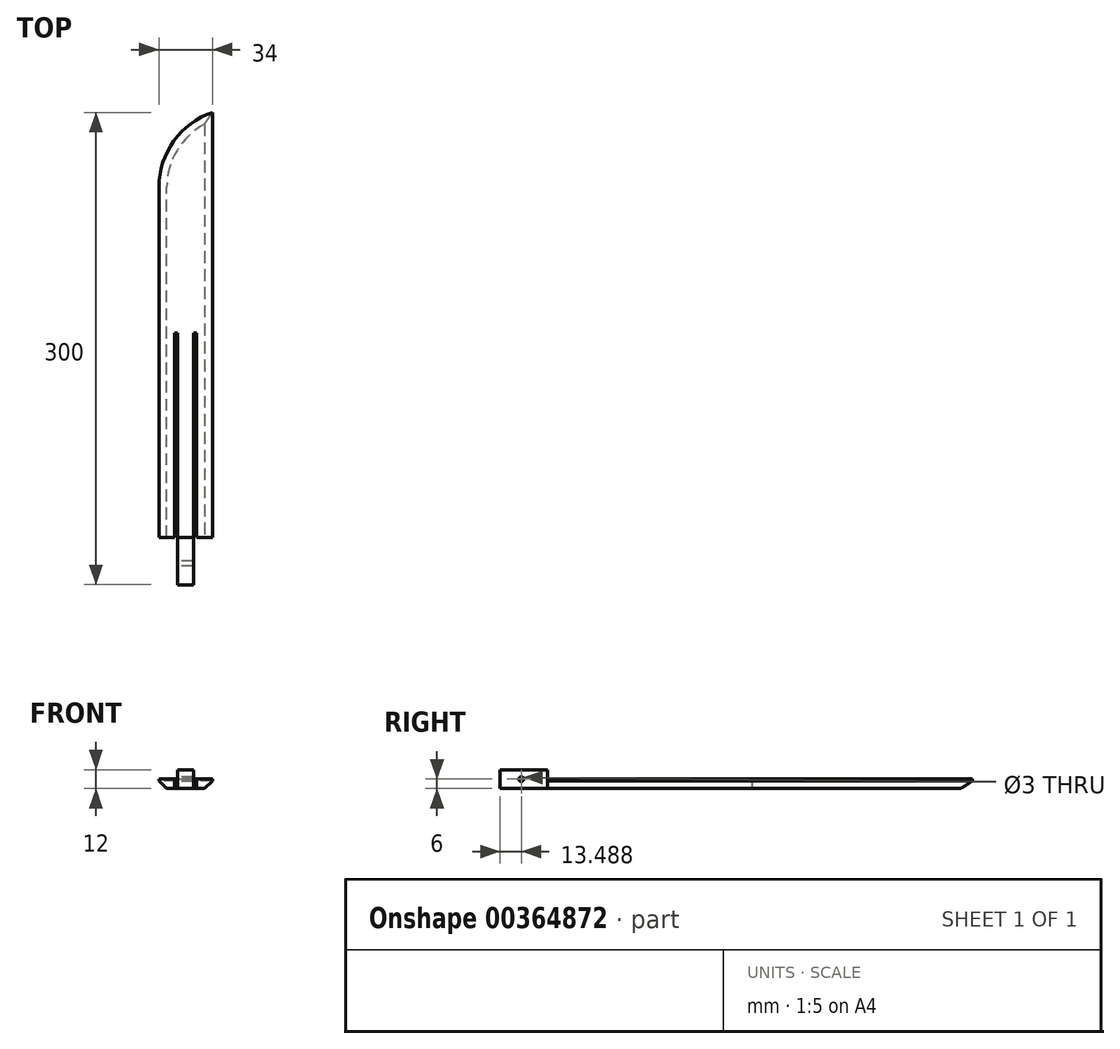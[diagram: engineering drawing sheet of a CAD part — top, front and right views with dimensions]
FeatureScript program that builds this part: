
annotation { "Feature Type Name" : "Feature", "Feature Type Description" : "" }
export const myFeature = defineFeature(function(context is Context, id is Id, definition is map)
    precondition{}
    {
        {
            var Q0;
            Q0=qCreatedBy(makeId("Top.planeOp"),FACE);
            var sketch = newSketch(context, id + "F0", { "sketchPlane" : qUnion([Q0])});
            skLineSegment(sketch, "E0.bottom", {"start": v(-19.09, 227.5) * mm, "end": v(14.91, 227.5) * mm});
            skLineSegment(sketch, "E0.left", {"start": v(-19.09, 227.5) * mm, "end": v(-19.09, -42.5) * mm});
            skLineSegment(sketch, "E0.right", {"start": v(14.91, 227.5) * mm, "end": v(14.91, -42.5) * mm});
            skLineSegment(sketch, "E1.top", {"start": v(-9.09, 87.5) * mm, "end": v(-7.09, 87.5) * mm});
            skLineSegment(sketch, "E1.left", {"start": v(-9.09, -42.5) * mm, "end": v(-9.09, 87.5) * mm});
            skLineSegment(sketch, "E1.right", {"start": v(-7.09, -72.5) * mm, "end": v(-7.09, 87.5) * mm});
            skLineSegment(sketch, "E2.top", {"start": v(2.91, 87.5) * mm, "end": v(4.91, 87.5) * mm});
            skLineSegment(sketch, "E2.left", {"start": v(2.91, -72.5) * mm, "end": v(2.91, 87.5) * mm});
            skLineSegment(sketch, "E2.right", {"start": v(4.91, -42.5) * mm, "end": v(4.91, 87.5) * mm});
            skLineSegment(sketch, "E3.trimOffspring", {"start": v(-7.09, -72.5) * mm, "end": v(2.91, -72.5) * mm});
            skLineSegment(sketch, "E4.top", {"start": v(-19.09, -42.5) * mm, "end": v(-9.09, -42.5) * mm});
            skLineSegment(sketch, "E5.top", {"start": v(4.91, -42.5) * mm, "end": v(14.91, -42.5) * mm});
            skSolve(sketch);
        }
        {
            var Q0;
            Q0=makeQuery(id+"F0.imprint","IMPRINT",FACE,{"disambiguationData":[TD([[makeQuery(id+"F0.imprint","IMPRINT",EDGE,{"derivedFrom":sQuery(id+"F0.wireOp",EDGE,"E0.bottom")}),-1.0]])]});
            extrude(context, id + "F1", {"entities" : qUnion([Q0]), "depth" : 6 * mm});
        }
        {
            var Q0;
            Q0=makeQuery(id+"F1.opExtrude","SWEPT_EDGE",EDGE,{"disambiguationData":[OSD([sQuery(id+"F0.wireOp",EDGE,"E0.bottom"),sQuery(id+"F0.wireOp",EDGE,"E0.left")])]});
            fillet(context, id + "F2", {"entities" : qUnion([Q0]), "radius" : 50 * mm, "tangentPropagation" : true, "allowEdgeOverflow" : false});
        }
        {
            var Q0;
            Q0=makeQuery(id+"F1.opExtrude","CAP_FACE",FACE,{"disambiguationData":[OSD([sQuery(id+"F0.wireOp",EDGE,"E0.bottom"),sQuery(id+"F0.wireOp",EDGE,"E0.left"),sQuery(id+"F0.wireOp",EDGE,"E0.right"),sQuery(id+"F0.wireOp",EDGE,"E1.top"),sQuery(id+"F0.wireOp",EDGE,"E1.left"),sQuery(id+"F0.wireOp",EDGE,"E1.right"),sQuery(id+"F0.wireOp",EDGE,"E2.top"),sQuery(id+"F0.wireOp",EDGE,"E2.left"),sQuery(id+"F0.wireOp",EDGE,"E2.right"),sQuery(id+"F0.wireOp",EDGE,"E3.trimOffspring"),sQuery(id+"F0.wireOp",EDGE,"E4.top"),sQuery(id+"F0.wireOp",EDGE,"E5.top")])],"isStart":false});
            var sketch = newSketch(context, id + "F3", { "sketchPlane" : qUnion([Q0])});
            skLineSegment(sketch, "E6.bottom", {"start": v(-7.09, -42.5) * mm, "end": v(2.91, -42.5) * mm});
            skLineSegment(sketch, "E6.top", {"start": v(-7.09, -72.5) * mm, "end": v(2.91, -72.5) * mm});
            skLineSegment(sketch, "E6.left", {"start": v(-7.09, -42.5) * mm, "end": v(-7.09, -72.5) * mm});
            skLineSegment(sketch, "E6.right", {"start": v(2.91, -42.5) * mm, "end": v(2.91, -72.5) * mm});
            skSolve(sketch);
        }
        {
            var Q0;
            Q0 = qSketchRegion(id + "F3", true);
            extrude(context, id + "F4", {"entities" : qUnion([Q0]), "operationType" : NewBodyOperationType.ADD, "depth" : 6 * mm});
        }
        {
            var Q0;
            Q0=makeQuery(id+"F4.boolean.opBoolean","MERGE",FACE,{"derivedFrom":[makeQuery(id+"F1.opExtrude","SWEPT_FACE",FACE,{"disambiguationData":[OSD([sQuery(id+"F0.wireOp",EDGE,"E1.right")])]}),makeQuery(id+"F4.opExtrude","SWEPT_FACE",FACE,{"disambiguationData":[OSD([sQuery(id+"F3.wireOp",EDGE,"E6.left")])]})]});
            var sketch = newSketch(context, id + "F5", { "sketchPlane" : qUnion([Q0])});
            skCircle(sketch, "E7", {"center": v(59, 6) * mm, "radius": 1.5 * mm});
            skPoint(sketch, "E7.centerSnap0", {"position": v(72.5, 6) * mm});
            skSolve(sketch);
        }
        {
            var Q0;
            Q0=makeQuery(id+"F5.imprint","IMPRINT",FACE,{"disambiguationData":[TD([[makeQuery(id+"F5.imprint","IMPRINT",EDGE,{"derivedFrom":sQuery(id+"F5.wireOp",EDGE,"E7")}),1.0]])]});
            extrude(context, id + "F6", {"entities" : qUnion([Q0]), "operationType" : NewBodyOperationType.REMOVE, "endBound" : BoundingType.UP_TO_NEXT, "oppositeDirection" : true, "depth" : 25 * mm});
        }
        {
            var Q0;
            Q0=makeQuery(id+"F1.opExtrude","CAP_EDGE",EDGE,{"disambiguationData":[OSD([sQuery(id+"F0.wireOp",EDGE,"E0.right")])],"isStart":true});
            var Q1;
            Q1=makeQuery(id+"F1.opExtrude","CAP_EDGE",EDGE,{"disambiguationData":[OSD([sQuery(id+"F0.wireOp",EDGE,"E0.left")])],"isStart":true});
            chamfer(context, id + "F7", {"entities" : qUnion([Q0, Q1]), "width" : 5 * mm, "tangentPropagation" : true});
        }
    });
